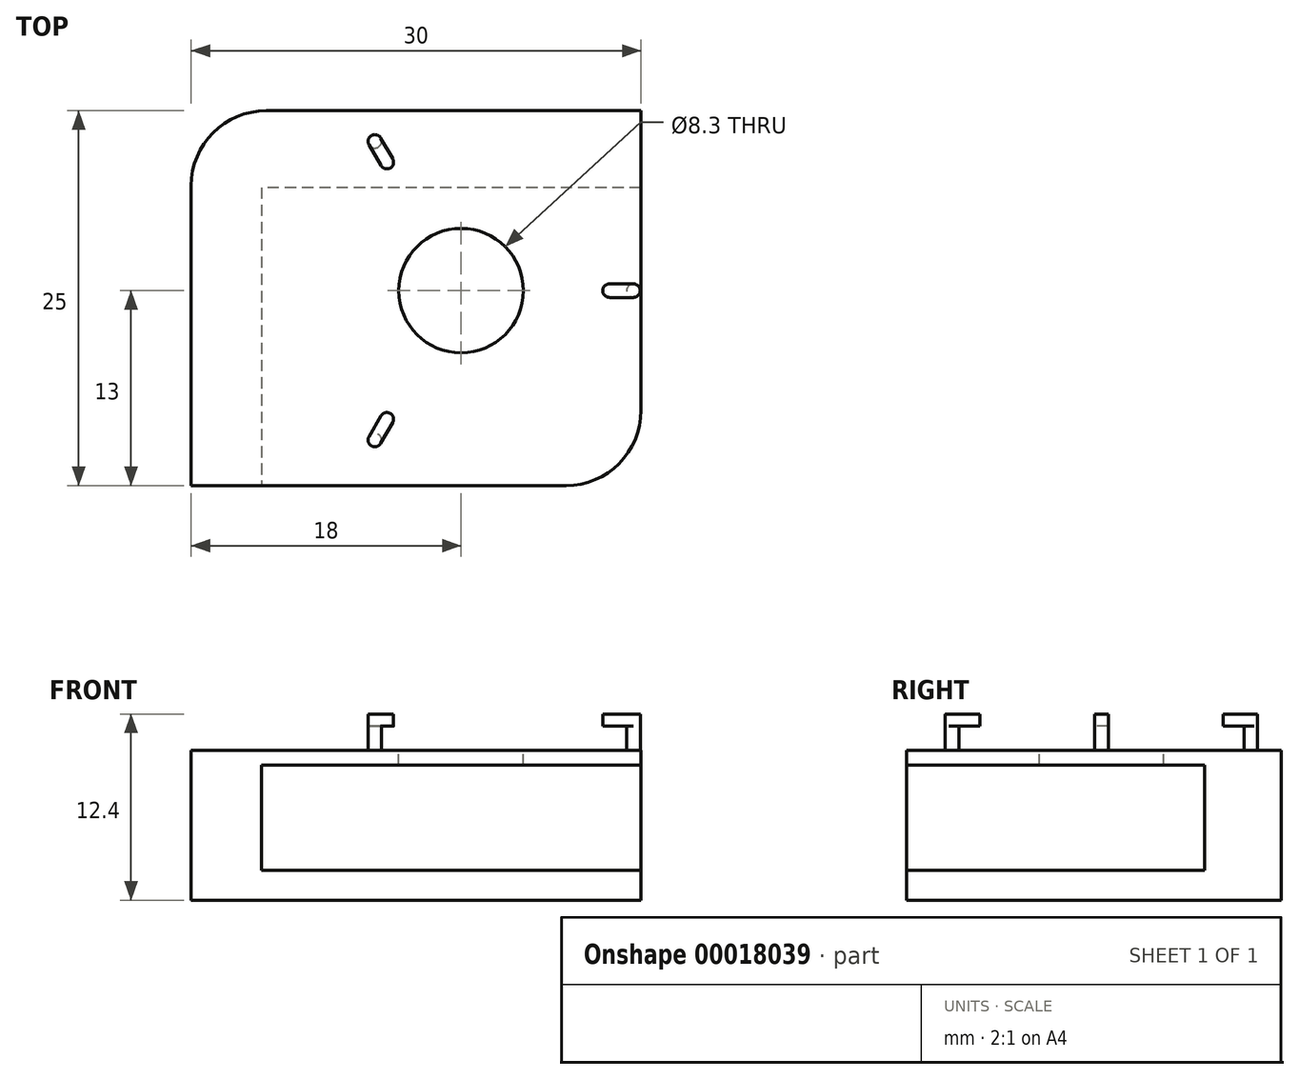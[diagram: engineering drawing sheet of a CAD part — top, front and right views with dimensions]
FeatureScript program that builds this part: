
annotation { "Feature Type Name" : "Feature", "Feature Type Description" : "" }
export const myFeature = defineFeature(function(context is Context, id is Id, definition is map)
    precondition{}
    {
        {
            var Q0;
            Q0=qCreatedBy(makeId("Top.planeOp"),FACE);
            var sketch = newSketch(context, id + "F0", { "sketchPlane" : qUnion([Q0])});
            skLineSegment(sketch, "E0.bottom", {"start": v(-18, 12) * mm, "end": v(12, 12) * mm});
            skLineSegment(sketch, "E0.top", {"start": v(-18, -13) * mm, "end": v(12, -13) * mm});
            skLineSegment(sketch, "E0.left", {"start": v(-18, 12) * mm, "end": v(-18, -13) * mm});
            skLineSegment(sketch, "E0.right", {"start": v(12, 12) * mm, "end": v(12, -13) * mm});
            skSolve(sketch);
        }
        {
            var Q0;
            Q0 = qSketchRegion(id + "F0", true);
            extrude(context, id + "F1", {"entities" : qUnion([Q0]), "depth" : 10 * mm});
        }
        {
            var Q0;
            Q0=makeQuery(id+"F1.opExtrude","SWEPT_FACE",FACE,{"disambiguationData":[OSD([sQuery(id+"F0.wireOp",EDGE,"E0.top")])]});
            var sketch = newSketch(context, id + "F2", { "sketchPlane" : qUnion([Q0])});
            skLineSegment(sketch, "E1", {"start": v(12, 2) * mm, "end": v(-13.31, 2) * mm});
            skLineSegment(sketch, "E2", {"start": v(-13.31, 2) * mm, "end": v(-13.31, 9) * mm});
            skLineSegment(sketch, "E3", {"start": v(-13.31, 9) * mm, "end": v(12, 9) * mm});
            skLineSegment(sketch, "E4", {"start": v(12, 9) * mm, "end": v(12, 2) * mm});
            skSolve(sketch);
        }
        {
            var Q0;
            Q0 = qSketchRegion(id + "F2", true);
            extrude(context, id + "F3", {"entities" : qUnion([Q0]), "operationType" : NewBodyOperationType.REMOVE, "oppositeDirection" : true, "depth" : (8 + 5 + 6.88) * mm});
        }
        {
            var Q0;
            Q0=makeQuery(id+"F1.opExtrude","CAP_FACE",FACE,{"disambiguationData":[OSD([sQuery(id+"F0.wireOp",EDGE,"E0.bottom"),sQuery(id+"F0.wireOp",EDGE,"E0.top"),sQuery(id+"F0.wireOp",EDGE,"E0.left"),sQuery(id+"F0.wireOp",EDGE,"E0.right")])],"isStart":false});
            var sketch = newSketch(context, id + "F4", { "sketchPlane" : qUnion([Q0])});
            skCircle(sketch, "E5", {"center": v(0, 0) * mm, "radius": 4.15 * mm});
            skSolve(sketch);
        }
        {
            var Q0;
            Q0 = qSketchRegion(id + "F4", true);
            extrude(context, id + "F5", {"entities" : qUnion([Q0]), "operationType" : NewBodyOperationType.REMOVE, "endBound" : BoundingType.UP_TO_NEXT, "oppositeDirection" : true, "depth" : 15 * mm});
        }
        {
            var Q0;
            {var subQ0=sQuery(id+"F0.wireOp",EDGE,"E0.top");var subQ1=sQuery(id+"F0.wireOp",EDGE,"E0.right");Q0=makeQuery(id+"F3.boolean.opBoolean","SPLIT",EDGE,{"disambiguationData":[TD([makeQuery(id+"F3.opExtrude","SWEPT_FACE",FACE,{"disambiguationData":[OSD([sQuery(id+"F2.wireOp",EDGE,"E3")])]})])],"derivedFrom":makeQuery(id+"F1.opExtrude","SWEPT_EDGE",EDGE,{"disambiguationData":[OSD([subQ0,subQ1])]})});}
            var Q1;
            {var subQ0=sQuery(id+"F0.wireOp",EDGE,"E0.top");var subQ1=sQuery(id+"F0.wireOp",EDGE,"E0.right");Q1=makeQuery(id+"F3.boolean.opBoolean","SPLIT",EDGE,{"disambiguationData":[TD([makeQuery(id+"F3.opExtrude","SWEPT_FACE",FACE,{"disambiguationData":[OSD([sQuery(id+"F2.wireOp",EDGE,"E1")])]})])],"derivedFrom":makeQuery(id+"F1.opExtrude","SWEPT_EDGE",EDGE,{"disambiguationData":[OSD([subQ0,subQ1])]})});}
            var Q2;
            Q2=makeQuery(id+"F1.opExtrude","SWEPT_EDGE",EDGE,{"disambiguationData":[OSD([sQuery(id+"F0.wireOp",EDGE,"E0.bottom"),sQuery(id+"F0.wireOp",EDGE,"E0.left")])]});
            fillet(context, id + "F6", {"entities" : qUnion([Q0, Q1, Q2]), "radius" : 5 * mm, "tangentPropagation" : true, "allowEdgeOverflow" : false});
        }
        {
            var Q0;
            Q0=makeQuery(id+"F1.opExtrude","CAP_FACE",FACE,{"disambiguationData":[OSD([sQuery(id+"F0.wireOp",EDGE,"E0.bottom"),sQuery(id+"F0.wireOp",EDGE,"E0.top"),sQuery(id+"F0.wireOp",EDGE,"E0.left"),sQuery(id+"F0.wireOp",EDGE,"E0.right")])],"isStart":false});
            var sketch = newSketch(context, id + "F7", { "sketchPlane" : qUnion([Q0])});
            skCircle(sketch, "E6", {"center": v(11.5, 0) * mm, "radius": 0.45 * mm});
            skSolve(sketch);
        }
        {
            var Q0;
            Q0=makeQuery(id+"F7.imprint","IMPRINT",FACE,{"disambiguationData":[TD([[makeQuery(id+"F7.imprint","IMPRINT",EDGE,{"derivedFrom":sQuery(id+"F7.wireOp",EDGE,"E6")}),1.0]])]});
            extrude(context, id + "F8", {"entities" : qUnion([Q0]), "depth" : 1.6 * mm});
        }
        {
            var Q0;
            Q0=makeQuery(id+"F8.opExtrude","CAP_FACE",FACE,{"disambiguationData":[OSD([sQuery(id+"F7.wireOp",EDGE,"E6")])],"isStart":false});
            var sketch = newSketch(context, id + "F9", { "sketchPlane" : qUnion([Q0])});
            skArc(sketch, "E7", {"start": v(11.5, -0.45) * mm, "mid": v(11.95, 0) * mm, "end": v(11.5, 0.45) * mm});
            skArc(sketch, "E8", {"start": v(9.9, 0.45) * mm, "mid": v(9.45, 0) * mm, "end": v(9.9, -0.45) * mm});
            skLineSegment(sketch, "E9", {"start": v(9.9, 0.45) * mm, "end": v(11.5, 0.45) * mm});
            skLineSegment(sketch, "E10", {"start": v(11.5, -0.45) * mm, "end": v(9.9, -0.45) * mm});
            skSolve(sketch);
        }
        {
            var Q0;
            Q0 = qSketchRegion(id + "F9", true);
            extrude(context, id + "F10", {"entities" : qUnion([Q0]), "operationType" : NewBodyOperationType.ADD, "depth" : 0.8 * mm});
        }
        {
            var Q0;
            Q0=qCreatedBy(makeId("Front.planeOp"),FACE);
            var sketch = newSketch(context, id + "F11", { "sketchPlane" : qUnion([Q0])});
            skLineSegment(sketch, "E11", {"start": v(0, 10) * mm, "end": v(0, 9) * mm, "construction": true});
            skSolve(sketch);
        }
        {
            var Q0;
            Q0=makeQuery(id+"F8.opExtrude","SWEPT_BODY",BODY,{"disambiguationData":[OSD([sQuery(id+"F7.wireOp",EDGE,"E6")])]});
            var Q1;
            Q1=sQuery(id+"F11.wireOp",EDGE,"E11");
            circularPattern(context, id + "F12", {"entities" : qUnion([Q0]), "axis" : qUnion([Q1]), "angle" : 360 * degree, "instanceCount" : 3, "equalSpace" : true});
        }
    });
